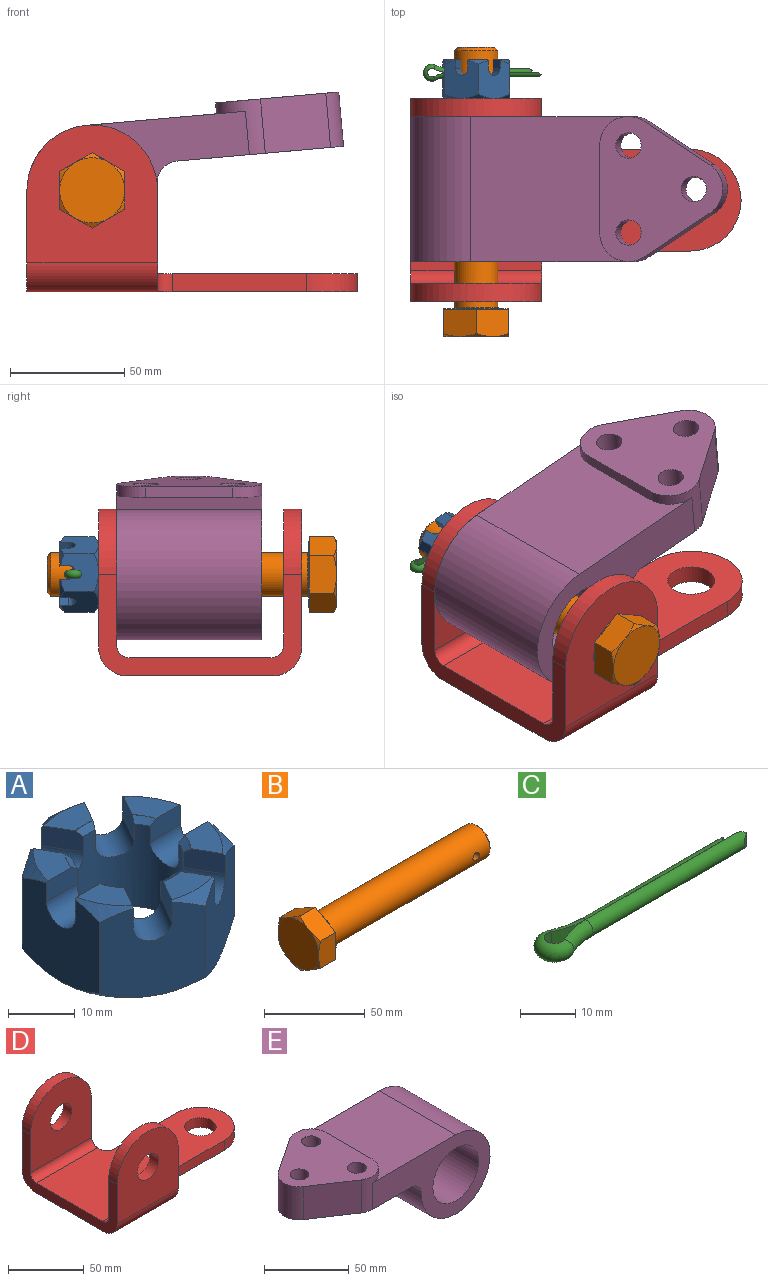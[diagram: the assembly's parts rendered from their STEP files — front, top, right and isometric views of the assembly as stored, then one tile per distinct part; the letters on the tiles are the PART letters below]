
ASSEMBLY  parts=5 mates=4
PART A: 64 faces, bbox 33x33x16.9 mm
  f0: cylinder r=8.33mm len=16.67mm, axis (0,0,1), area 599.6mm2, adj f8,f9,f10,f11,f12,f13,f14,f15
  f1: plane 28.58x28.58mm, normal (0,0,-1), area 356.3mm2, adj f32,f33,f34,f35,f36,f37,f51
  f2: plane 8.68x4.95mm, normal (0,0,1), area 30mm2, adj f12,f16,f41,f48
  f3: plane 7.52x6.81mm, normal (0,0,1), area 30mm2, adj f9,f13,f43,f49
  f4: plane 7.52x6.81mm, normal (0,0,1), area 30mm2, adj f8,f18,f39,f44
  f5: plane 7.52x6.81mm, normal (0,0,1), area 30mm2, adj f11,f15,f42,f46
  f6: plane 7.52x6.81mm, normal (0,0,1), area 30mm2, adj f10,f17,f40,f47
  f7: plane 8.68x4.95mm, normal (0,0,1), area 30mm2, adj f14,f19,f38,f45
  f8: plane 6.56x3.71mm, normal (0,-1,0), area 23.4mm2, adj f0,f4,f22,f26,f39,f44,f62,f63
  f9: plane 6.56x3.71mm, normal (0,1,0), area 23.4mm2, adj f0,f3,f22,f26,f43,f49,f52,f53
  f10: plane 6.56x3.71mm, normal (0,1,0), area 23.4mm2, adj f0,f6,f25,f27,f40,f47,f56,f57
  f11: plane 6.56x3.71mm, normal (0,-1,0), area 23.4mm2, adj f0,f5,f25,f27,f42,f46,f58,f59
  f12: plane 5.69x3.71mm, normal (0.87,0.5,0), area 23.4mm2, adj f0,f2,f23,f28,f41,f48,f54,f55
  f13: plane 5.69x3.71mm, normal (-0.87,-0.5,0), area 23.4mm2, adj f0,f3,f23,f28,f43,f49,f52,f53
  f14: plane 5.69x3.71mm, normal (-0.87,-0.5,0), area 23.4mm2, adj f0,f7,f20,f29,f38,f45,f60,f61
  f15: plane 5.69x3.71mm, normal (0.87,0.5,0), area 23.4mm2, adj f0,f5,f20,f29,f42,f46,f58,f59
  f16: plane 5.69x3.71mm, normal (-0.87,0.5,0), area 23.4mm2, adj f0,f2,f24,f30,f41,f48,f54,f55
  f17: plane 5.69x3.71mm, normal (0.87,-0.5,0), area 23.4mm2, adj f0,f6,f24,f30,f40,f47,f56,f57
  f18: plane 5.69x3.71mm, normal (-0.87,0.5,0), area 23.4mm2, adj f0,f4,f21,f31,f39,f44,f62,f63
  f19: plane 5.69x3.71mm, normal (0.87,-0.5,0), area 23.4mm2, adj f0,f7,f21,f31,f38,f45,f60,f61
  f20: plane 16.62x14.29mm, normal (-0.5,0.87,0), area 220.6mm2, adj f14,f15,f21,f25,f29,f32,f33,f38
  f21: plane 16.62x14.29mm, normal (0.5,0.87,0), area 220.6mm2, adj f18,f19,f20,f22,f31,f33,f34,f38
  f22: plane 16.63x16.51mm, normal (1,0,0), area 220.6mm2, adj f8,f9,f21,f23,f26,f34,f35,f39
  f23: plane 16.62x14.29mm, normal (0.5,-0.87,0), area 220.6mm2, adj f12,f13,f22,f24,f28,f35,f36,f41
  f24: plane 16.62x14.29mm, normal (-0.5,-0.87,0), area 220.6mm2, adj f16,f17,f23,f25,f30,f36,f37,f40
  f25: plane 16.63x16.51mm, normal (-1,0,0), area 220.6mm2, adj f10,f11,f20,f24,f27,f32,f37,f40
  f26: cylinder r=3.05mm len=6.53mm, axis (1,0,0), area 59.8mm2, adj f0,f8,f9,f22
  f27: cylinder r=3.05mm len=6.53mm, axis (1,0,0), area 59.8mm2, adj f0,f10,f11,f25
  f28: cylinder r=3.05mm len=8.7mm, axis (-0.5,0.87,0), area 59.8mm2, adj f0,f12,f13,f23
  f29: cylinder r=3.05mm len=8.7mm, axis (-0.5,0.87,0), area 59.8mm2, adj f0,f14,f15,f20
  f30: cylinder r=3.05mm len=8.7mm, axis (0.5,0.87,0), area 59.8mm2, adj f0,f16,f17,f24
  f31: cylinder r=3.05mm len=8.7mm, axis (0.5,0.87,0), area 59.8mm2, adj f0,f18,f19,f21
  f32: cone r=14.29mm half-angle=49.2deg, axis (0,0,1), area 14.5mm2, adj f1,f20,f25
  f33: cone r=14.29mm half-angle=49.2deg, axis (0,0,1), area 14.5mm2, adj f1,f20,f21
  f34: cone r=14.29mm half-angle=49.2deg, axis (0,0,1), area 14.5mm2, adj f1,f21,f22
  f35: cone r=14.29mm half-angle=49.2deg, axis (0,0,1), area 14.5mm2, adj f1,f22,f23
  f36: cone r=14.29mm half-angle=49.2deg, axis (0,0,1), area 14.5mm2, adj f1,f23,f24
  f37: cone r=14.29mm half-angle=49.2deg, axis (0,0,1), area 14.5mm2, adj f1,f24,f25
  f38: cone r=14.29mm half-angle=49.2deg, axis (0,0,-1), area 13.6mm2, adj f7,f14,f19,f20,f21
  f39: cone r=14.29mm half-angle=49.2deg, axis (0,0,-1), area 13.6mm2, adj f4,f8,f18,f21,f22
  f40: cone r=14.29mm half-angle=49.2deg, axis (0,0,-1), area 13.6mm2, adj f6,f10,f17,f24,f25
  f41: cone r=14.29mm half-angle=49.2deg, axis (0,0,-1), area 13.6mm2, adj f2,f12,f16,f23,f24
  f42: cone r=14.29mm half-angle=49.2deg, axis (0,0,-1), area 13.6mm2, adj f5,f11,f15,f20,f25
  f43: cone r=14.29mm half-angle=49.2deg, axis (0,0,-1), area 13.6mm2, adj f3,f9,f13,f22,f23
  f44: cone r=8.21mm half-angle=55deg, axis (0,0,1), area 0.1mm2, adj f4,f8,f18,f63
  f45: cone r=8.21mm half-angle=55deg, axis (0,0,1), area 0.1mm2, adj f7,f14,f19,f60
  f46: cone r=8.21mm half-angle=55deg, axis (0,0,1), area 0.1mm2, adj f5,f11,f15,f58
  f47: cone r=8.21mm half-angle=55deg, axis (0,0,1), area 0.1mm2, adj f6,f10,f17,f56
  f48: cone r=8.21mm half-angle=55deg, axis (0,0,1), area 0.1mm2, adj f2,f12,f16,f54
  f49: cone r=8.21mm half-angle=55deg, axis (0,0,1), area 0.1mm2, adj f3,f9,f13,f52
  f50: cone r=9.53mm half-angle=55deg, axis (0,0,-1), area 81.6mm2, adj f0,f51
  f51: cylinder r=9.53mm len=19.05mm, axis (0,0,1), area 1.5mm2, adj f1,f50
  f52: cone r=9.53mm half-angle=55deg, axis (0,0,-1), area 0.1mm2, adj f9,f13,f49,f53
  f53: cone r=8.33mm half-angle=55deg, axis (0,0,1), area 4.5mm2, adj f0,f9,f13,f52
  f54: cone r=9.53mm half-angle=55deg, axis (0,0,-1), area 0.1mm2, adj f12,f16,f48,f55
  f55: cone r=8.33mm half-angle=55deg, axis (0,0,1), area 4.5mm2, adj f0,f12,f16,f54
  f56: cone r=9.53mm half-angle=55deg, axis (0,0,-1), area 0.1mm2, adj f10,f17,f47,f57
  f57: cone r=8.33mm half-angle=55deg, axis (0,0,1), area 4.5mm2, adj f0,f10,f17,f56
  f58: cone r=9.53mm half-angle=55deg, axis (0,0,-1), area 0.1mm2, adj f11,f15,f46,f59
  f59: cone r=8.33mm half-angle=55deg, axis (0,0,1), area 4.5mm2, adj f0,f11,f15,f58
  f60: cone r=9.53mm half-angle=55deg, axis (0,0,-1), area 0.1mm2, adj f14,f19,f45,f61
  f61: cone r=8.33mm half-angle=55deg, axis (0,0,1), area 4.5mm2, adj f0,f14,f19,f60
  f62: cone r=8.33mm half-angle=55deg, axis (0,0,1), area 4.5mm2, adj f0,f8,f18,f63
  f63: cone r=9.53mm half-angle=55deg, axis (0,0,-1), area 0.1mm2, adj f8,f18,f44,f62
PART B: 26 faces, bbox 126.6x33x33 mm
  f0: plane 28.58x28.58mm, normal (1,0,0), area 325.1mm2, adj f10,f24
  f1: cylinder r=9.53mm len=112.28mm, axis (-1,0,0), area 6683.8mm2, adj f2,f24,f25
  f2: cone r=8.01mm half-angle=45deg, axis (-1,0,0), area 117.9mm2, adj f1,f3
  f3: plane 16.03x16.03mm, normal (1,0,0), area 201.7mm2, adj f2
  f4: plane 12.37x7.14mm, normal (1,0,0), area 11mm2, adj f10,f18,f23
  f5: plane 14.29x4.12mm, normal (1,0,0), area 11mm2, adj f10,f22,f23
  f6: plane 12.37x7.14mm, normal (1,0,0), area 11mm2, adj f10,f21,f22
  f7: plane 12.37x7.14mm, normal (1,0,0), area 11mm2, adj f10,f20,f21
  f8: plane 14.29x4.12mm, normal (1,0,0), area 11mm2, adj f10,f19,f20
  f9: plane 12.37x7.14mm, normal (1,0,0), area 11mm2, adj f10,f18,f19
  f10: cylinder r=14.29mm len=28.58mm, axis (-1,0,0), area 34.2mm2, adj f0,f4,f5,f6,f7,f8,f9
  f11: plane 28.58x28.58mm, normal (-1,0,0), area 641.3mm2, adj f12,f13,f14,f15,f16,f17
  f12: cone r=14.29mm half-angle=60deg, axis (1,0,0), area 12.7mm2, adj f11,f22,f23
  f13: cone r=14.29mm half-angle=60deg, axis (1,0,0), area 12.7mm2, adj f11,f21,f22
  f14: cone r=14.29mm half-angle=60deg, axis (1,0,0), area 12.7mm2, adj f11,f20,f21
  f15: cone r=14.29mm half-angle=60deg, axis (1,0,0), area 12.7mm2, adj f11,f19,f20
  f16: cone r=14.29mm half-angle=60deg, axis (1,0,0), area 12.7mm2, adj f11,f18,f23
  f17: cone r=14.29mm half-angle=60deg, axis (1,0,0), area 12.7mm2, adj f11,f18,f19
  f18: plane 16.51x11.89mm, normal (0,1,0), area 188.9mm2, adj f4,f9,f16,f17,f19,f23
  f19: plane 14.29x11.89mm, normal (0,0.5,-0.87), area 188.9mm2, adj f8,f9,f15,f17,f18,f20
  f20: plane 14.29x11.89mm, normal (0,-0.5,-0.87), area 188.9mm2, adj f7,f8,f14,f15,f19,f21
  f21: plane 16.51x11.89mm, normal (0,-1,0), area 188.9mm2, adj f6,f7,f13,f14,f20,f22
  f22: plane 14.29x11.89mm, normal (0,-0.5,0.87), area 188.9mm2, adj f5,f6,f12,f13,f21,f23
  f23: plane 14.29x11.89mm, normal (0,0.5,0.87), area 188.9mm2, adj f4,f5,f12,f16,f18,f22
  f24: torus R=10.03mm, axis (1,0,0), area 48.7mm2, adj f0,f1
  f25: cylinder r=2.38mm len=19.05mm, axis (0,-1,0), area 285mm2, adj f1
PART C: 14 faces, bbox 52x8x3.7 mm
  f0: plane 38.67x3.7mm, normal (0,1,0), area 143.1mm2, adj f1,f2,f13
  f1: cylinder r=1.85mm len=40mm, axis (1,0,0), area 227.7mm2, adj f0,f3,f12,f13
  f2: cylinder r=16.37mm len=7.19mm, axis (0,0,-1), area 27.5mm2, adj f0,f3,f4
  f3: torus R=16.37mm, axis (0,0,-1), area 40.1mm2, adj f1,f2,f5
  f4: cylinder r=1.85mm len=3.7mm, axis (0,0,1), area 27.8mm2, adj f2,f5,f6
  f5: torus R=1.85mm, axis (0,0,1), area 71.2mm2, adj f3,f4,f7
  f6: cylinder r=16.37mm len=7.19mm, axis (0,0,-1), area 27.5mm2, adj f4,f7,f9
  f7: torus R=16.37mm, axis (0,0,-1), area 40.1mm2, adj f5,f6,f8
  f8: cylinder r=1.85mm len=36mm, axis (1,0,0), area 204.5mm2, adj f7,f9,f10,f11
  f9: plane 34.67x3.7mm, normal (0,-1,0), area 128.3mm2, adj f6,f8,f10
  f10: plane 3.7x1.33mm, normal (0.57,-0.82,0), area 5.7mm2, adj f8,f9,f11
  f11: plane 3.2x1.31mm, normal (0.58,0.82,0), area 3.6mm2, adj f8,f10
  f12: plane 3.2x1.31mm, normal (0.58,-0.82,0), area 3.6mm2, adj f1,f13
  f13: plane 3.7x1.33mm, normal (0.57,0.82,0), area 5.7mm2, adj f0,f1,f12
PART D: 24 faces, bbox 144.5x88.9x73 mm
  f0: plane 44.45x15.88mm, normal (1,0,0), area 387.8mm2, adj f9,f10,f11,f16,f17,f19,f20,f23
  f1: plane 88.9x44.45mm, normal (-1,0,0), area 1229.3mm2, adj f10,f11,f12,f14,f15,f16,f17,f19
  f2: plane 44.45x15.88mm, normal (1,0,0), area 387.8mm2, adj f3,f10,f11,f12,f14,f15,f21,f22
  f3: cylinder r=6.35mm len=7.94mm, axis (0,0,-1), area 79.2mm2, adj f2,f4,f10,f11
  f4: plane 58.75x7.94mm, normal (0,-1,0), area 466.3mm2, adj f3,f5,f10,f11
  f5: cylinder r=22.23mm len=44.45mm, axis (0,0,-1), area 554.2mm2, adj f4,f6,f10,f11
  f6: plane 58.75x7.94mm, normal (0,1,0), area 466.3mm2, adj f5,f9,f10,f11
  f7: cylinder r=10.33mm len=20.65mm, axis (0,0,-1), area 514.9mm2, adj f10,f11
  f8: cylinder r=10.33mm len=20.65mm, axis (0,0,-1), area 514.9mm2, adj f10,f11
  f9: cylinder r=6.35mm len=7.94mm, axis (0,0,-1), area 79.2mm2, adj f0,f6,f10,f11
  f10: plane 144.48x61.91mm, normal (0,0,1), area 6555.4mm2, adj f0,f1,f2,f3,f4,f5,f6,f7
  f11: plane 144.48x63.5mm, normal (0,0,-1), area 6646.1mm2, adj f0,f1,f2,f3,f4,f5,f6,f7
  f12: cylinder r=28.57mm len=57.15mm, axis (0,1,0), area 712.6mm2, adj f1,f2,f14,f15
  f13: cylinder r=9.92mm len=19.85mm, axis (0,1,0), area 494.9mm2, adj f14,f15
  f14: plane 60.33x57.15mm, normal (0,-1,0), area 2787.8mm2, adj f1,f2,f12,f13,f21
  f15: plane 59.53x57.15mm, normal (0,1,0), area 2742.4mm2, adj f1,f2,f12,f13,f22
  f16: plane 59.53x57.15mm, normal (0,-1,0), area 2742.4mm2, adj f0,f1,f17,f18,f23
  f17: cylinder r=28.57mm len=57.15mm, axis (0,-1,0), area 712.6mm2, adj f0,f1,f16,f19
  f18: cylinder r=9.92mm len=19.85mm, axis (0,-1,0), area 494.9mm2, adj f16,f19
  f19: plane 60.33x57.15mm, normal (0,1,0), area 2787.8mm2, adj f0,f1,f17,f18,f20
  f20: cylinder r=12.7mm len=57.15mm, axis (-1,0,0), area 1140.1mm2, adj f0,f1,f11,f19
  f21: cylinder r=12.7mm len=57.15mm, axis (-1,0,0), area 1140.1mm2, adj f1,f2,f11,f14
  f22: cylinder r=5.56mm len=57.15mm, axis (1,0,0), area 498.8mm2, adj f1,f2,f10,f15
  f23: cylinder r=5.56mm len=57.15mm, axis (1,0,0), area 498.8mm2, adj f0,f1,f10,f16
PART E: 17 faces, bbox 139.8x63.5x61.9 mm
  f0: cylinder r=9.53mm len=63.5mm, axis (0,1,0), area 950.1mm2, adj f1,f4,f5,f6
  f1: cylinder r=28.57mm len=63.5mm, axis (0,1,0), area 8550.7mm2, adj f0,f2,f5,f6
  f2: plane 69.85x63.5mm, normal (0,0,1), area 3698.3mm2, adj f1,f5,f6,f7,f8,f14
  f3: cylinder r=19.05mm len=63.5mm, axis (0,1,0), area 7600.6mm2, adj f5,f6
  f4: plane 73.15x63.5mm, normal (0,0,-1), area 3399.6mm2, adj f0,f5,f6,f8,f9,f10,f11,f12
  f5: plane 98.43x57.15mm, normal (0,-1,0), area 2406.1mm2, adj f0,f1,f2,f3,f4,f14
  f6: plane 98.43x57.15mm, normal (0,1,0), area 2406.1mm2, adj f0,f1,f2,f3,f4,f8
  f7: plane 38.1x4.78mm, normal (1,0,0), area 181.9mm2, adj f2,f8,f14,f16
  f8: cylinder r=12.7mm len=23.83mm, axis (0,0,-1), area 272.6mm2, adj f2,f4,f6,f7,f9,f16
  f9: plane 28.7x23.83mm, normal (-0.55,0.83,0), area 820.7mm2, adj f4,f8,f10,f16
  f10: cylinder r=12.7mm len=23.83mm, axis (0,0,-1), area 596mm2, adj f4,f9,f11,f16
  f11: plane 28.7x23.83mm, normal (-0.55,-0.83,0), area 820.7mm2, adj f4,f10,f14,f16
  f12: cylinder r=5.56mm len=23.83mm, axis (0,0,-1), area 832.7mm2, adj f4,f16
  f13: cylinder r=5.56mm len=23.83mm, axis (0,0,-1), area 832.7mm2, adj f4,f16
  f14: cylinder r=12.7mm len=23.83mm, axis (0,0,-1), area 272.6mm2, adj f2,f4,f5,f7,f11,f16
  f15: cylinder r=5.56mm len=23.83mm, axis (0,0,-1), area 832.7mm2, adj f4,f16
  f16: plane 63.5x54.1mm, normal (0,0,1), area 2120.7mm2, adj f7,f8,f9,f10,f11,f12,f13,f14
PLACE A rot(axis=(-0.75,0.47,0.47),106deg) t=(-18.36,28.11,97.37)mm
PLACE B rot(axis=(0,0,1),90deg) t=(-18.36,-92.98,97.37)mm
PLACE C t=(-37.83,22.48,97.37)mm
PLACE D t=(-46.93,-69.74,52.92)mm fixed
PLACE E rot(axis=(0.04,0,-1),180deg) t=(-18.36,-60.22,97.37)mm
MATE slider B.f25 <-> C.f8  axis (1,0,0) through (-28,22.48,97.37)mm
MATE revolute D.f12 <-> E.f1  axis (0,-1,0) through (-18.36,3.28,97.37)mm
MATE revolute D.f12 <-> A.f0  axis (0,1,0) through (-18.36,11.22,97.37)mm
MATE slider D.f12 <-> B.f1  axis (0,-1,0) through (-18.36,-77.68,97.37)mm
